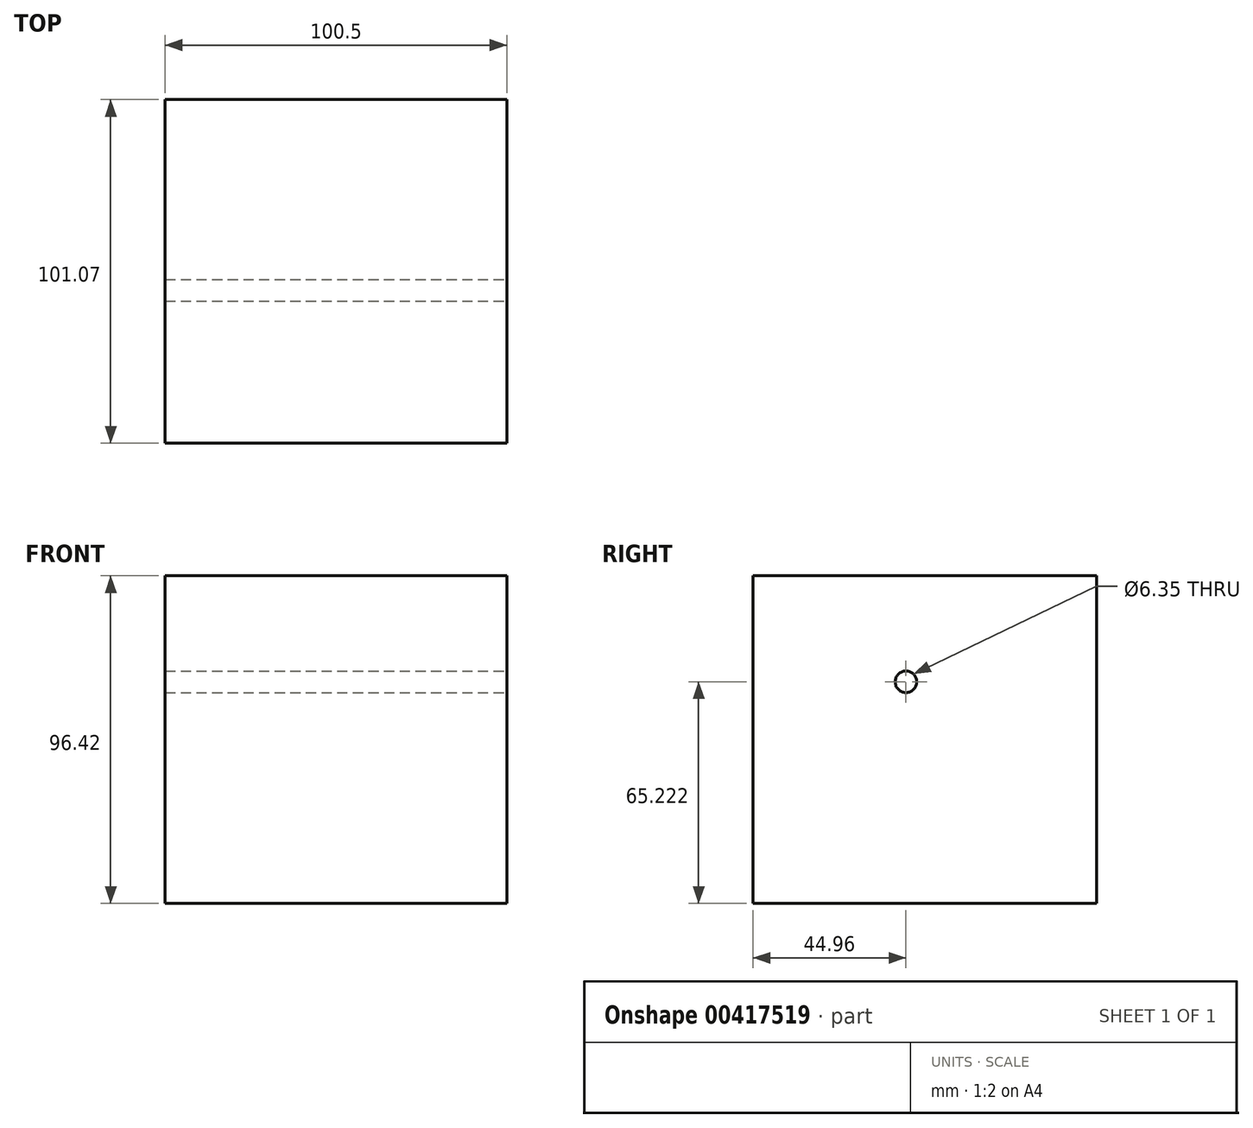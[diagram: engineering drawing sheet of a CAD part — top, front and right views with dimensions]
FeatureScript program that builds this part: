
annotation { "Feature Type Name" : "Feature", "Feature Type Description" : "" }
export const myFeature = defineFeature(function(context is Context, id is Id, definition is map)
    precondition{}
    {
        {
            var Q0;
            Q0=qCreatedBy(makeId("Right.planeOp"),FACE);
            var sketch = newSketch(context, id + "F0", { "sketchPlane" : qUnion([Q0])});
            skLineSegment(sketch, "E0.bottom", {"start": v(-44.96, -29.82) * mm, "end": v(56.1, -29.82) * mm});
            skLineSegment(sketch, "E0.top", {"start": v(-44.96, 66.6) * mm, "end": v(56.1, 66.6) * mm});
            skLineSegment(sketch, "E0.left", {"start": v(-44.96, -29.82) * mm, "end": v(-44.96, 66.6) * mm});
            skLineSegment(sketch, "E0.right", {"start": v(56.1, -29.82) * mm, "end": v(56.1, 66.6) * mm});
            skSolve(sketch);
        }
        {
            var Q0;
            Q0 = qSketchRegion(id + "F0", true);
            extrude(context, id + "F1", {"entities" : qUnion([Q0]), "depth" : 100.5 * mm});
        }
        {
            var Q0;
            Q0=makeQuery(id+"F1.opExtrude","CAP_FACE",FACE,{"disambiguationData":[OSD([sQuery(id+"F0.wireOp",EDGE,"E0.bottom"),sQuery(id+"F0.wireOp",EDGE,"E0.top"),sQuery(id+"F0.wireOp",EDGE,"E0.left"),sQuery(id+"F0.wireOp",EDGE,"E0.right")])],"isStart":false});
            var sketch = newSketch(context, id + "F2", { "sketchPlane" : qUnion([Q0])});
            skSolve(sketch);
        }
        {
            var Q0;
            Q0=makeQuery(id+"F2.imprint","IMPRINT",FACE,{"disambiguationData":[TD([[makeQuery(id+"F2.imprint","IMPRINT",EDGE,{"derivedFrom":makeQuery(id+"F1.opExtrude","CAP_EDGE",EDGE,{"disambiguationData":[OSD([sQuery(id+"F0.wireOp",EDGE,"E0.bottom")])],"isStart":false})}),1.0]])]});
            var sketch = newSketch(context, id + "F3", { "sketchPlane" : qUnion([Q0])});
            skPoint(sketch, "E1", {"position": v(0, 35.4) * mm});
            skSolve(sketch);
        }
        {
            var Q0;
            Q0=sQuery(id+"F3.wireOp",VERTEX,"E1");
            var Q1;
            Q1=makeQuery(id+"F1.opExtrude","SWEPT_BODY",BODY,{"disambiguationData":[OSD([sQuery(id+"F0.wireOp",EDGE,"E0.bottom"),sQuery(id+"F0.wireOp",EDGE,"E0.top"),sQuery(id+"F0.wireOp",EDGE,"E0.left"),sQuery(id+"F0.wireOp",EDGE,"E0.right")])]});
            hole(context, id + "F4", {"style" : HoleStyle.SIMPLE, "endStyle" : HoleEndStyle.THROUGH, "holeDiameter" : 6.35 * mm, "isTappedThrough" : true, "tappedDepth" : 12.7 * mm, "tapClearance" : 3, "locations" : qUnion([Q0]), "scope" : qUnion([Q1])});
        }
    });
